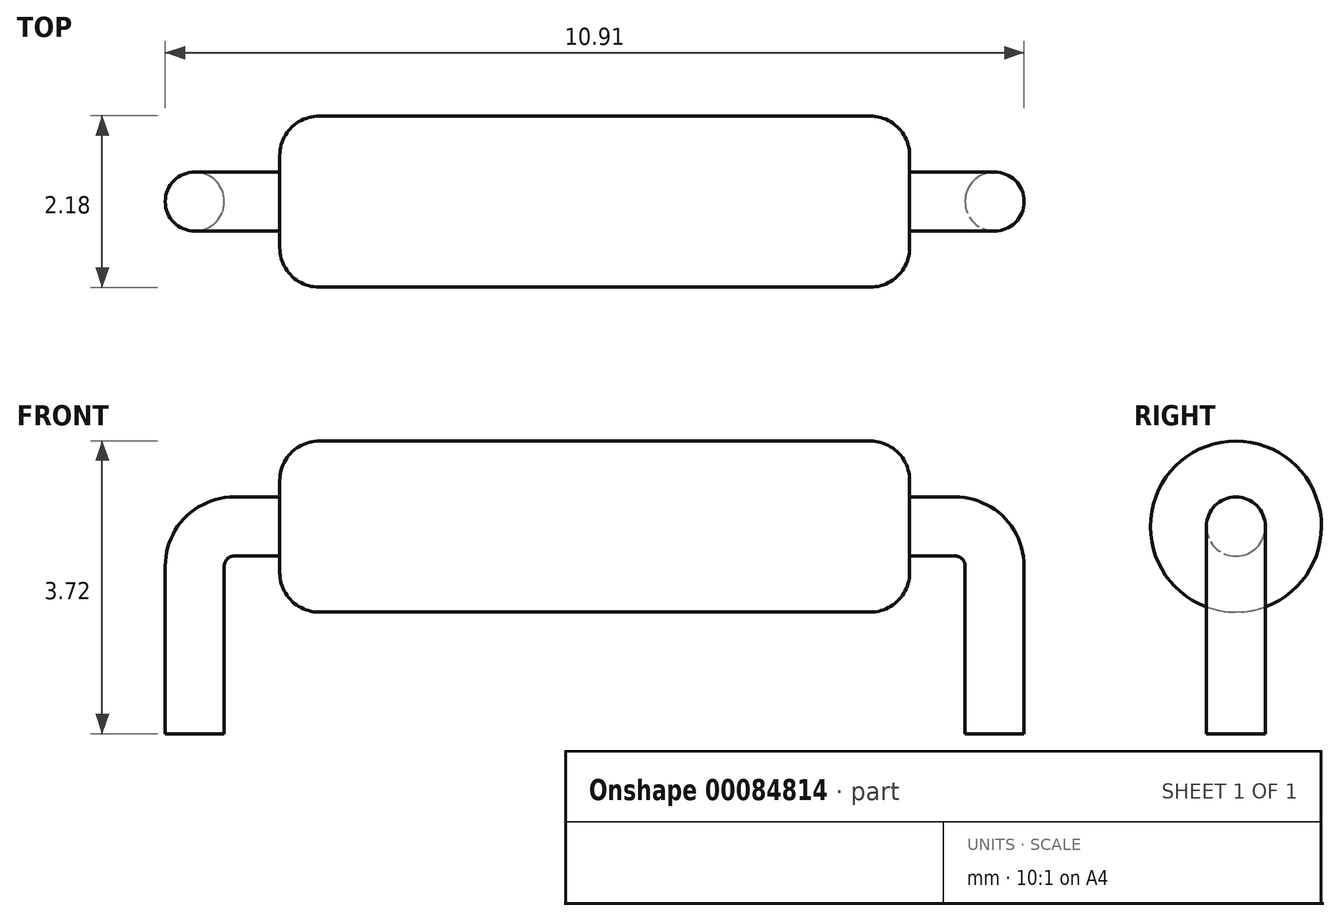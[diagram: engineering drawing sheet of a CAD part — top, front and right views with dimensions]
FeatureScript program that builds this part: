
annotation { "Feature Type Name" : "Feature", "Feature Type Description" : "" }
export const myFeature = defineFeature(function(context is Context, id is Id, definition is map)
    precondition{}
    {
        {
            var Q0;
            Q0=qCreatedBy(makeId("Front.planeOp"),FACE);
            var sketch = newSketch(context, id + "F0", { "sketchPlane" : qUnion([Q0])});
            skLineSegment(sketch, "E0", {"start": v(-12.3, 33.9) * mm, "end": v(-1.96, 33.9) * mm, "construction": true});
            skLineSegment(sketch, "E1.bottom", {"start": v(-11.4, 33.9) * mm, "end": v(-3.4, 33.9) * mm});
            skLineSegment(sketch, "E1.top", {"start": v(-10.9, 34.99) * mm, "end": v(-3.9, 34.99) * mm});
            skLineSegment(sketch, "E1.left", {"start": v(-11.4, 33.9) * mm, "end": v(-11.4, 34.49) * mm});
            skLineSegment(sketch, "E1.right", {"start": v(-3.4, 33.9) * mm, "end": v(-3.4, 34.49) * mm});
            skPoint(sketch, "E2.visualSharp", {"position": v(-11.4, 34.99) * mm});
            skArc(sketch, "E2.filletArc", {"start": v(-10.9, 34.99) * mm, "mid": v(-11.26, 34.84) * mm, "end": v(-11.4, 34.49) * mm});
            skPoint(sketch, "E3.visualSharp", {"position": v(-3.4, 34.99) * mm});
            skArc(sketch, "E3.filletArc", {"start": v(-3.4, 34.49) * mm, "mid": v(-3.55, 34.84) * mm, "end": v(-3.9, 34.99) * mm});
            skPoint(sketch, "E4", {"position": v(-11.4, 33.9) * mm});
            skPoint(sketch, "E5", {"position": v(-3.4, 33.9) * mm});
            skLineSegment(sketch, "E6", {"start": v(-11.4, 33.9) * mm, "end": v(-11.99, 33.9) * mm});
            skLineSegment(sketch, "E7", {"start": v(-12.49, 33.4) * mm, "end": v(-12.49, 31.27) * mm});
            skPoint(sketch, "E8.visualSharp", {"position": v(-12.49, 33.9) * mm});
            skArc(sketch, "E8.filletArc", {"start": v(-11.99, 33.9) * mm, "mid": v(-12.34, 33.76) * mm, "end": v(-12.49, 33.4) * mm});
            skLineSegment(sketch, "E9", {"start": v(-3.4, 33.9) * mm, "end": v(-2.83, 33.9) * mm});
            skLineSegment(sketch, "E10", {"start": v(-2.33, 33.4) * mm, "end": v(-2.33, 31.27) * mm});
            skPoint(sketch, "E11.visualSharp", {"position": v(-2.33, 33.9) * mm});
            skArc(sketch, "E11.filletArc", {"start": v(-2.33, 33.4) * mm, "mid": v(-2.47, 33.76) * mm, "end": v(-2.83, 33.9) * mm});
            skSolve(sketch);
        }
        {
            var Q0;
            Q0=makeQuery(id+"F0.imprint","IMPRINT",FACE,{"disambiguationData":[TD([[makeQuery(id+"F0.imprint","IMPRINT",EDGE,{"derivedFrom":sQuery(id+"F0.wireOp",EDGE,"E1.bottom")}),1.0]])]});
            var Q1;
            Q1=sQuery(id+"F0.wireOp",EDGE,"E0");
            revolve(context, id + "F1", {"entities" : qUnion([Q0]), "axis" : qUnion([Q1]), "revolveType" : RevolveType.FULL});
        }
        {
            var Q0;
            Q0=makeQuery(id+"F1.opRevolve","SWEPT_FACE",FACE,{"disambiguationData":[OSD([sQuery(id+"F0.wireOp",EDGE,"E1.left")])]});
            var Q1;
            Q1=sQuery(id+"F0.wireOp",EDGE,"E6");
            sweep(context, id + "F2", {"operationType" : NewBodyOperationType.REMOVE, "profiles" : qUnion([Q0]), "path" : qUnion([Q1])});
        }
        {
            var Q0;
            Q0=makeQuery(id+"F1.opRevolve","SWEPT_FACE",FACE,{"disambiguationData":[OSD([sQuery(id+"F0.wireOp",EDGE,"E1.left")])]});
            var sketch = newSketch(context, id + "F3", { "sketchPlane" : qUnion([Q0])});
            skCircle(sketch, "E12", {"center": v(0, 33.9) * mm, "radius": 0.38 * mm});
            skSolve(sketch);
        }
        {
            var Q0;
            Q0=makeQuery(id+"F3.imprint","IMPRINT",FACE,{"disambiguationData":[TD([[makeQuery(id+"F3.imprint","IMPRINT",EDGE,{"derivedFrom":sQuery(id+"F3.wireOp",EDGE,"E12")}),1.0]])]});
            var Q1;
            Q1=sQuery(id+"F0.wireOp",EDGE,"E6");
            var Q2;
            Q2=sQuery(id+"F0.wireOp",EDGE,"E8.filletArc");
            var Q3;
            Q3=sQuery(id+"F0.wireOp",EDGE,"E7");
            sweep(context, id + "F4", {"profiles" : qUnion([Q0]), "path" : qUnion([Q1, Q2, Q3])});
        }
        {
            var Q0;
            Q0=makeQuery(id+"F1.opRevolve","SWEPT_FACE",FACE,{"disambiguationData":[OSD([sQuery(id+"F0.wireOp",EDGE,"E1.right")])]});
            var sketch = newSketch(context, id + "F5", { "sketchPlane" : qUnion([Q0])});
            skCircle(sketch, "E13", {"center": v(0, 33.9) * mm, "radius": 0.38 * mm});
            skSolve(sketch);
        }
        {
            var Q0;
            Q0=makeQuery(id+"F5.imprint","IMPRINT",FACE,{"disambiguationData":[TD([[makeQuery(id+"F5.imprint","IMPRINT",EDGE,{"derivedFrom":sQuery(id+"F5.wireOp",EDGE,"E13")}),1.0]])]});
            var Q1;
            Q1=sQuery(id+"F0.wireOp",EDGE,"E9");
            var Q2;
            Q2=sQuery(id+"F0.wireOp",EDGE,"E11.filletArc");
            var Q3;
            Q3=sQuery(id+"F0.wireOp",EDGE,"E10");
            sweep(context, id + "F6", {"profiles" : qUnion([Q0]), "path" : qUnion([Q1, Q2, Q3])});
        }
    });
